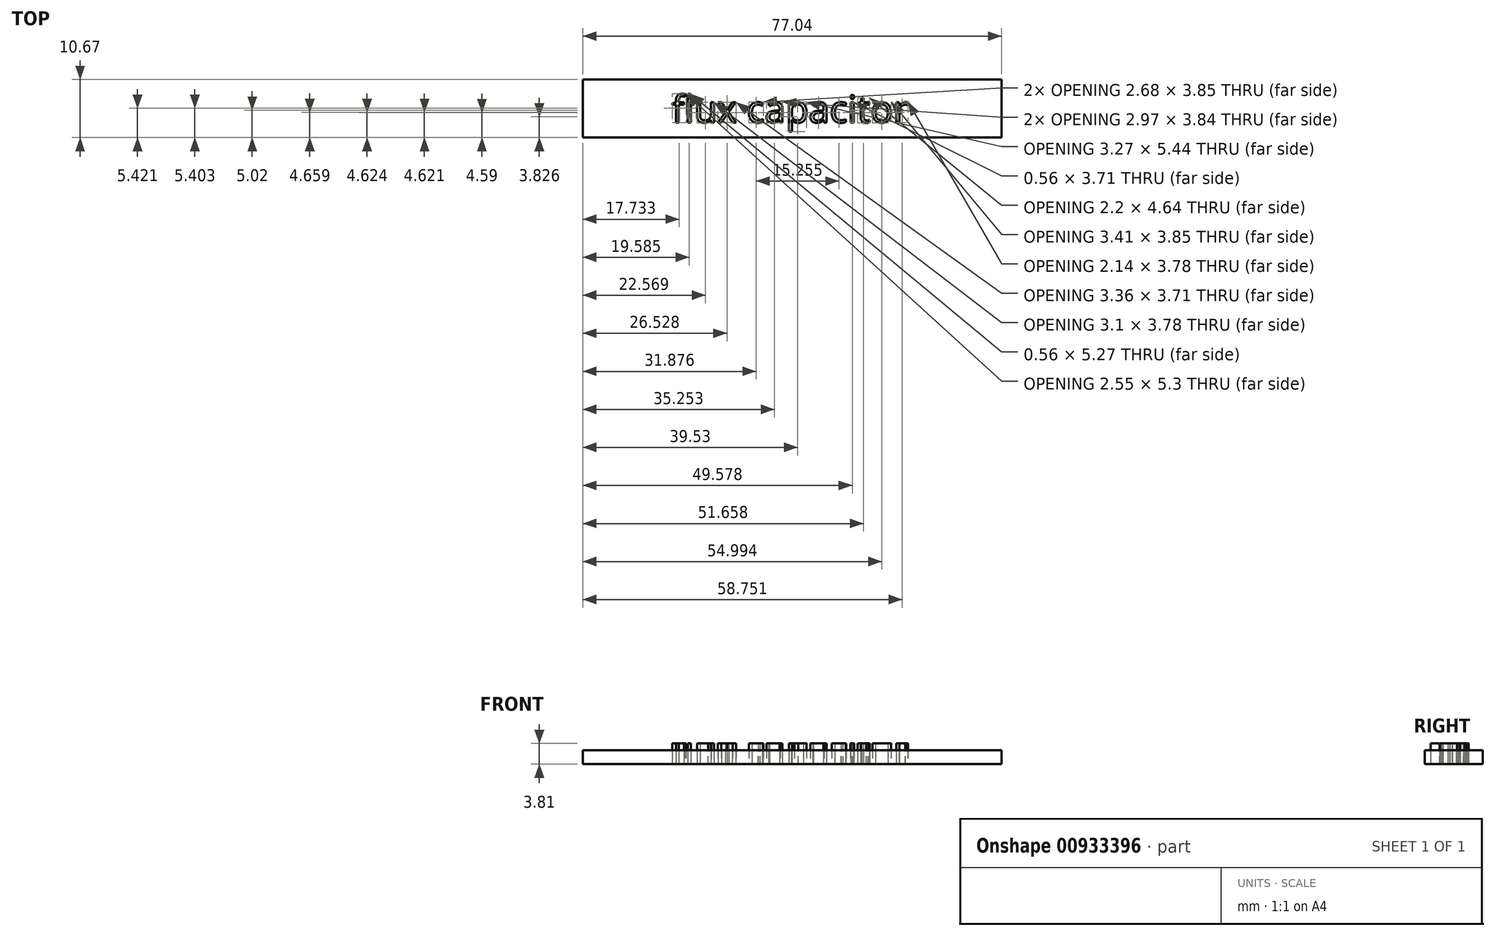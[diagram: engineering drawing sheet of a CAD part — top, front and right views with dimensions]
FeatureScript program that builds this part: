
annotation { "Feature Type Name" : "Feature", "Feature Type Description" : "" }
export const myFeature = defineFeature(function(context is Context, id is Id, definition is map)
    precondition{}
    {
        {
            var Q0;
            Q0=qCreatedBy(makeId("Top.planeOp"),FACE);
            var sketch = newSketch(context, id + "F0", { "sketchPlane" : qUnion([Q0])});
            skLineSegment(sketch, "E0.bottom", {"start": v(-41.36, -7.76) * mm, "end": v(35.68, -7.76) * mm});
            skLineSegment(sketch, "E0.top", {"start": v(-41.36, 2.9) * mm, "end": v(35.68, 2.9) * mm});
            skLineSegment(sketch, "E0.left", {"start": v(-41.36, -7.76) * mm, "end": v(-41.36, 2.9) * mm});
            skLineSegment(sketch, "E0.right", {"start": v(35.68, -7.76) * mm, "end": v(35.68, 2.9) * mm});
            skText(sketch, "E1", { "text": "flux capacitor", "fontName": "OpenSans-Regular.ttf"});
            const initialGuessF0  = {"E1": [-0.025, -0.00499, 1, 0, 0.00499]};
            skSetInitialGuess(sketch, initialGuessF0);
            skSolve(sketch);
        }
        {
            var Q0;
            Q0 = qSketchRegion(id + "F0", true);
            var Q1;
            Q1=makeQuery(id+"F0.imprint","IMPRINT",FACE,{"disambiguationData":[TD([[makeQuery(id+"F0.imprint","IMPRINT",EDGE,{"derivedFrom":sQuery(id+"F0.wireOp",EDGE,"E1.sketch_text.stroke-84")}),1.0]])]});
            var Q2;
            Q2=makeQuery(id+"F0.imprint","IMPRINT",FACE,{"disambiguationData":[TD([[makeQuery(id+"F0.imprint","IMPRINT",EDGE,{"derivedFrom":sQuery(id+"F0.wireOp",EDGE,"E1.sketch_text.stroke-108")}),1.0]])]});
            var Q3;
            Q3=makeQuery(id+"F0.imprint","IMPRINT",FACE,{"disambiguationData":[TD([[makeQuery(id+"F0.imprint","IMPRINT",EDGE,{"derivedFrom":sQuery(id+"F0.wireOp",EDGE,"E1.sketch_text.stroke-136")}),1.0]])]});
            var Q4;
            Q4=makeQuery(id+"F0.imprint","IMPRINT",FACE,{"disambiguationData":[TD([[makeQuery(id+"F0.imprint","IMPRINT",EDGE,{"derivedFrom":sQuery(id+"F0.wireOp",EDGE,"E1.sketch_text.stroke-199")}),1.0]])]});
            extrude(context, id + "F1", {"entities" : qUnion([Q0, Q1, Q2, Q3, Q4]), "depth" : 2.54 * mm, "offsetDistance" : 25.4 * mm});
        }
        {
            var Q0;
            Q0=makeQuery(id+"F0.imprint","IMPRINT",FACE,{"disambiguationData":[TD([[makeQuery(id+"F0.imprint","IMPRINT",EDGE,{"derivedFrom":sQuery(id+"F0.wireOp",EDGE,"E1.sketch_text.stroke-0")}),-1.0]])]});
            var Q1;
            Q1=makeQuery(id+"F0.imprint","IMPRINT",FACE,{"disambiguationData":[TD([[makeQuery(id+"F0.imprint","IMPRINT",EDGE,{"derivedFrom":sQuery(id+"F0.wireOp",EDGE,"E1.sketch_text.stroke-17")}),-1.0]])]});
            var Q2;
            Q2=makeQuery(id+"F0.imprint","IMPRINT",FACE,{"disambiguationData":[TD([[makeQuery(id+"F0.imprint","IMPRINT",EDGE,{"derivedFrom":sQuery(id+"F0.wireOp",EDGE,"E1.sketch_text.stroke-21")}),-1.0]])]});
            var Q3;
            Q3=makeQuery(id+"F0.imprint","IMPRINT",FACE,{"disambiguationData":[TD([[makeQuery(id+"F0.imprint","IMPRINT",EDGE,{"derivedFrom":sQuery(id+"F0.wireOp",EDGE,"E1.sketch_text.stroke-38")}),-1.0]])]});
            var Q4;
            Q4=makeQuery(id+"F0.imprint","IMPRINT",FACE,{"disambiguationData":[TD([[makeQuery(id+"F0.imprint","IMPRINT",EDGE,{"derivedFrom":sQuery(id+"F0.wireOp",EDGE,"E1.sketch_text.stroke-50")}),-1.0]])]});
            var Q5;
            Q5=makeQuery(id+"F0.imprint","IMPRINT",FACE,{"disambiguationData":[TD([[makeQuery(id+"F0.imprint","IMPRINT",EDGE,{"derivedFrom":sQuery(id+"F0.wireOp",EDGE,"E1.sketch_text.stroke-65")}),-1.0]])]});
            var Q6;
            Q6=makeQuery(id+"F0.imprint","IMPRINT",FACE,{"disambiguationData":[TD([[makeQuery(id+"F0.imprint","IMPRINT",EDGE,{"derivedFrom":sQuery(id+"F0.wireOp",EDGE,"E1.sketch_text.stroke-92")}),-1.0]])]});
            var Q7;
            Q7=makeQuery(id+"F0.imprint","IMPRINT",FACE,{"disambiguationData":[TD([[makeQuery(id+"F0.imprint","IMPRINT",EDGE,{"derivedFrom":sQuery(id+"F0.wireOp",EDGE,"E1.sketch_text.stroke-117")}),-1.0]])]});
            var Q8;
            Q8=makeQuery(id+"F0.imprint","IMPRINT",FACE,{"disambiguationData":[TD([[makeQuery(id+"F0.imprint","IMPRINT",EDGE,{"derivedFrom":sQuery(id+"F0.wireOp",EDGE,"E1.sketch_text.stroke-144")}),-1.0]])]});
            var Q9;
            Q9=makeQuery(id+"F0.imprint","IMPRINT",FACE,{"disambiguationData":[TD([[makeQuery(id+"F0.imprint","IMPRINT",EDGE,{"derivedFrom":sQuery(id+"F0.wireOp",EDGE,"E1.sketch_text.stroke-159")}),-1.0]])]});
            var Q10;
            Q10=makeQuery(id+"F0.imprint","IMPRINT",FACE,{"disambiguationData":[TD([[makeQuery(id+"F0.imprint","IMPRINT",EDGE,{"derivedFrom":sQuery(id+"F0.wireOp",EDGE,"E1.sketch_text.stroke-163")}),-1.0]])]});
            var Q11;
            Q11=makeQuery(id+"F0.imprint","IMPRINT",FACE,{"disambiguationData":[TD([[makeQuery(id+"F0.imprint","IMPRINT",EDGE,{"derivedFrom":sQuery(id+"F0.wireOp",EDGE,"E1.sketch_text.stroke-171")}),-1.0]])]});
            var Q12;
            Q12=makeQuery(id+"F0.imprint","IMPRINT",FACE,{"disambiguationData":[TD([[makeQuery(id+"F0.imprint","IMPRINT",EDGE,{"derivedFrom":sQuery(id+"F0.wireOp",EDGE,"E1.sketch_text.stroke-190")}),-1.0]])]});
            var Q13;
            Q13=makeQuery(id+"F0.imprint","IMPRINT",FACE,{"disambiguationData":[TD([[makeQuery(id+"F0.imprint","IMPRINT",EDGE,{"derivedFrom":sQuery(id+"F0.wireOp",EDGE,"E1.sketch_text.stroke-207")}),-1.0]])]});
            extrude(context, id + "F2", {"entities" : qUnion([Q0, Q1, Q2, Q3, Q4, Q5, Q6, Q7, Q8, Q9, Q10, Q11, Q12, Q13]), "depth" : 3.8 * mm, "offsetDistance" : 25.4 * mm});
        }
    });
